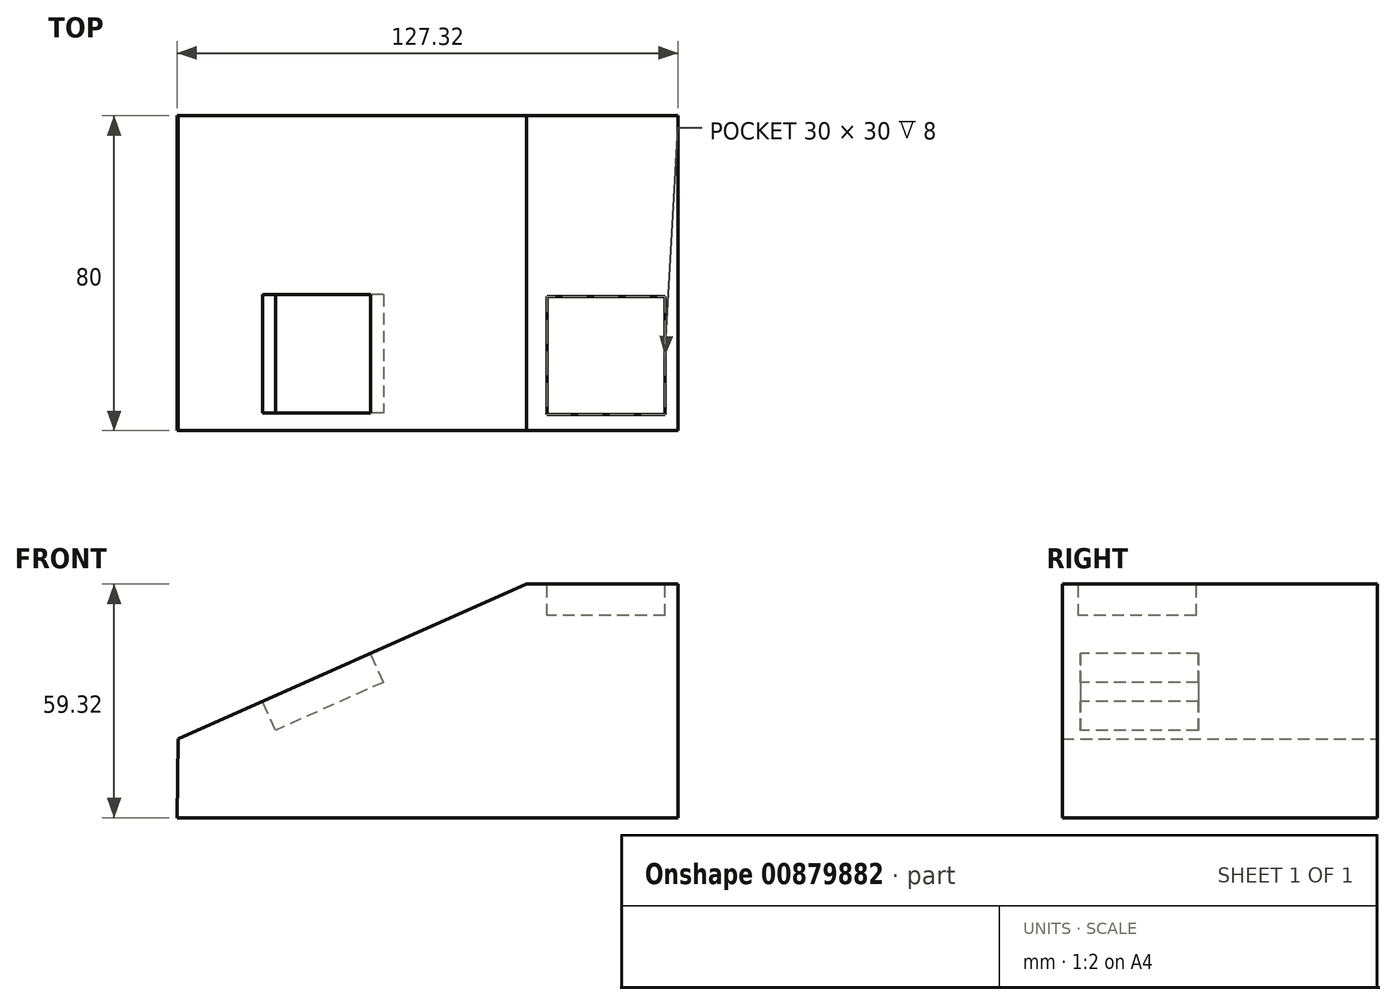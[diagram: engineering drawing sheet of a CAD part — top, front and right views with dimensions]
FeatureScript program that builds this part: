
annotation { "Feature Type Name" : "Feature", "Feature Type Description" : "" }
export const myFeature = defineFeature(function(context is Context, id is Id, definition is map)
    precondition{}
    {
        {
            var Q0;
            Q0=qCreatedBy(makeId("Front.planeOp"),FACE);
            var sketch = newSketch(context, id + "F0", { "sketchPlane" : qUnion([Q0])});
            skLineSegment(sketch, "E0", {"start": v(-62.36, -41.96) * mm, "end": v(64.96, -41.96) * mm});
            skLineSegment(sketch, "E1", {"start": v(64.96, -41.96) * mm, "end": v(64.96, 17.36) * mm});
            skLineSegment(sketch, "E2", {"start": v(64.96, 17.36) * mm, "end": v(26.48, 17.36) * mm});
            skLineSegment(sketch, "E3", {"start": v(26.48, 17.36) * mm, "end": v(-62.07, -22) * mm});
            skLineSegment(sketch, "E4", {"start": v(-62.07, -22) * mm, "end": v(-62.36, -41.96) * mm});
            skSolve(sketch);
        }
        {
            var Q0;
            Q0 = qSketchRegion(id + "F0", true);
            extrude(context, id + "F1", {"entities" : qUnion([Q0]), "depth" : 80 * mm, "offsetDistance" : 25 * mm});
        }
        {
            var Q0;
            Q0=makeQuery(id+"F1.opExtrude","SWEPT_FACE",FACE,{"disambiguationData":[OSD([sQuery(id+"F0.wireOp",EDGE,"E2")])]});
            var sketch = newSketch(context, id + "F2", { "sketchPlane" : qUnion([Q0])});
            skLineSegment(sketch, "E5.bottom", {"start": v(61.66, -45.92) * mm, "end": v(31.66, -45.92) * mm});
            skLineSegment(sketch, "E5.top", {"start": v(61.66, -75.92) * mm, "end": v(31.66, -75.92) * mm});
            skLineSegment(sketch, "E5.left", {"start": v(61.66, -45.92) * mm, "end": v(61.66, -75.92) * mm});
            skLineSegment(sketch, "E5.right", {"start": v(31.66, -45.92) * mm, "end": v(31.66, -75.92) * mm});
            skSolve(sketch);
        }
        {
            var Q0;
            Q0 = qSketchRegion(id + "F2", true);
            extrude(context, id + "F3", {"entities" : qUnion([Q0]), "operationType" : NewBodyOperationType.REMOVE, "oppositeDirection" : true, "depth" : 8 * mm, "offsetDistance" : 25 * mm});
        }
        {
            var Q0;
            Q0=makeQuery(id+"F1.opExtrude","SWEPT_FACE",FACE,{"disambiguationData":[OSD([sQuery(id+"F0.wireOp",EDGE,"E3")])]});
            var sketch = newSketch(context, id + "F4", { "sketchPlane" : qUnion([Q0])});
            skLineSegment(sketch, "E6.bottom", {"start": v(-12.14, -45.46) * mm, "end": v(-42.14, -45.46) * mm});
            skLineSegment(sketch, "E6.top", {"start": v(-12.14, -75.46) * mm, "end": v(-42.14, -75.46) * mm});
            skLineSegment(sketch, "E6.left", {"start": v(-12.14, -45.46) * mm, "end": v(-12.14, -75.46) * mm});
            skLineSegment(sketch, "E6.right", {"start": v(-42.14, -45.46) * mm, "end": v(-42.14, -75.46) * mm});
            skSolve(sketch);
        }
        {
            var Q0;
            Q0 = qSketchRegion(id + "F4", true);
            extrude(context, id + "F5", {"entities" : qUnion([Q0]), "operationType" : NewBodyOperationType.REMOVE, "oppositeDirection" : true, "depth" : 8 * mm, "offsetDistance" : 25 * mm});
        }
    });
